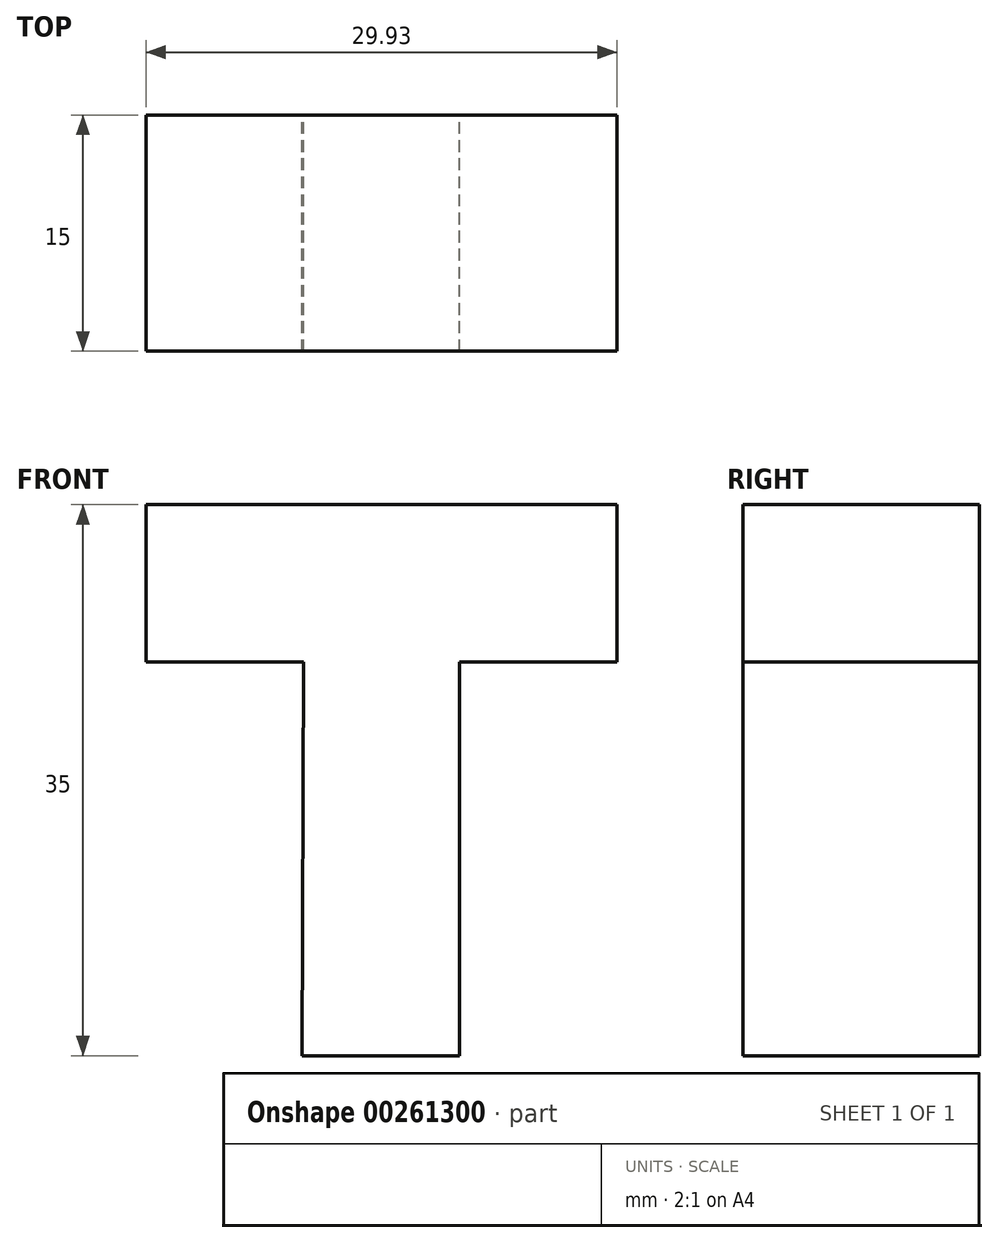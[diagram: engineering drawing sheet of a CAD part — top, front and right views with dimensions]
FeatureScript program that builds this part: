
annotation { "Feature Type Name" : "Feature", "Feature Type Description" : "" }
export const myFeature = defineFeature(function(context is Context, id is Id, definition is map)
    precondition{}
    {
        {
            var Q0;
            Q0=qCreatedBy(makeId("Front.planeOp"),FACE);
            var sketch = newSketch(context, id + "F0", { "sketchPlane" : qUnion([Q0])});
            skLineSegment(sketch, "E0", {"start": v(-5, 0) * mm, "end": v(0, 0) * mm});
            skLineSegment(sketch, "E1", {"start": v(0, 0) * mm, "end": v(5, 0) * mm});
            skLineSegment(sketch, "E2", {"start": v(5, 0) * mm, "end": v(5, 25) * mm});
            skLineSegment(sketch, "E3", {"start": v(5, 25) * mm, "end": v(15, 25) * mm});
            skLineSegment(sketch, "E4", {"start": v(15, 25) * mm, "end": v(15, 35) * mm});
            skLineSegment(sketch, "E5", {"start": v(15, 35) * mm, "end": v(0, 35) * mm});
            skLineSegment(sketch, "E6", {"start": v(0, 35) * mm, "end": v(-14.93, 35) * mm});
            skLineSegment(sketch, "E7", {"start": v(-14.93, 35) * mm, "end": v(-14.93, 25) * mm});
            skLineSegment(sketch, "E8", {"start": v(-14.93, 25) * mm, "end": v(-4.93, 25) * mm});
            skLineSegment(sketch, "E9", {"start": v(-4.93, 25) * mm, "end": v(-5, 0) * mm});
            skSolve(sketch);
        }
        {
            var Q0;
            Q0=makeQuery(id+"F0.imprint","IMPRINT",FACE,{"disambiguationData":[TD([[makeQuery(id+"F0.imprint","IMPRINT",EDGE,{"derivedFrom":sQuery(id+"F0.wireOp",EDGE,"E0")}),1.0]])]});
            extrude(context, id + "F1", {"entities" : qUnion([Q0]), "endBound" : BoundingType.SYMMETRIC, "depth" : 15 * mm});
        }
    });
